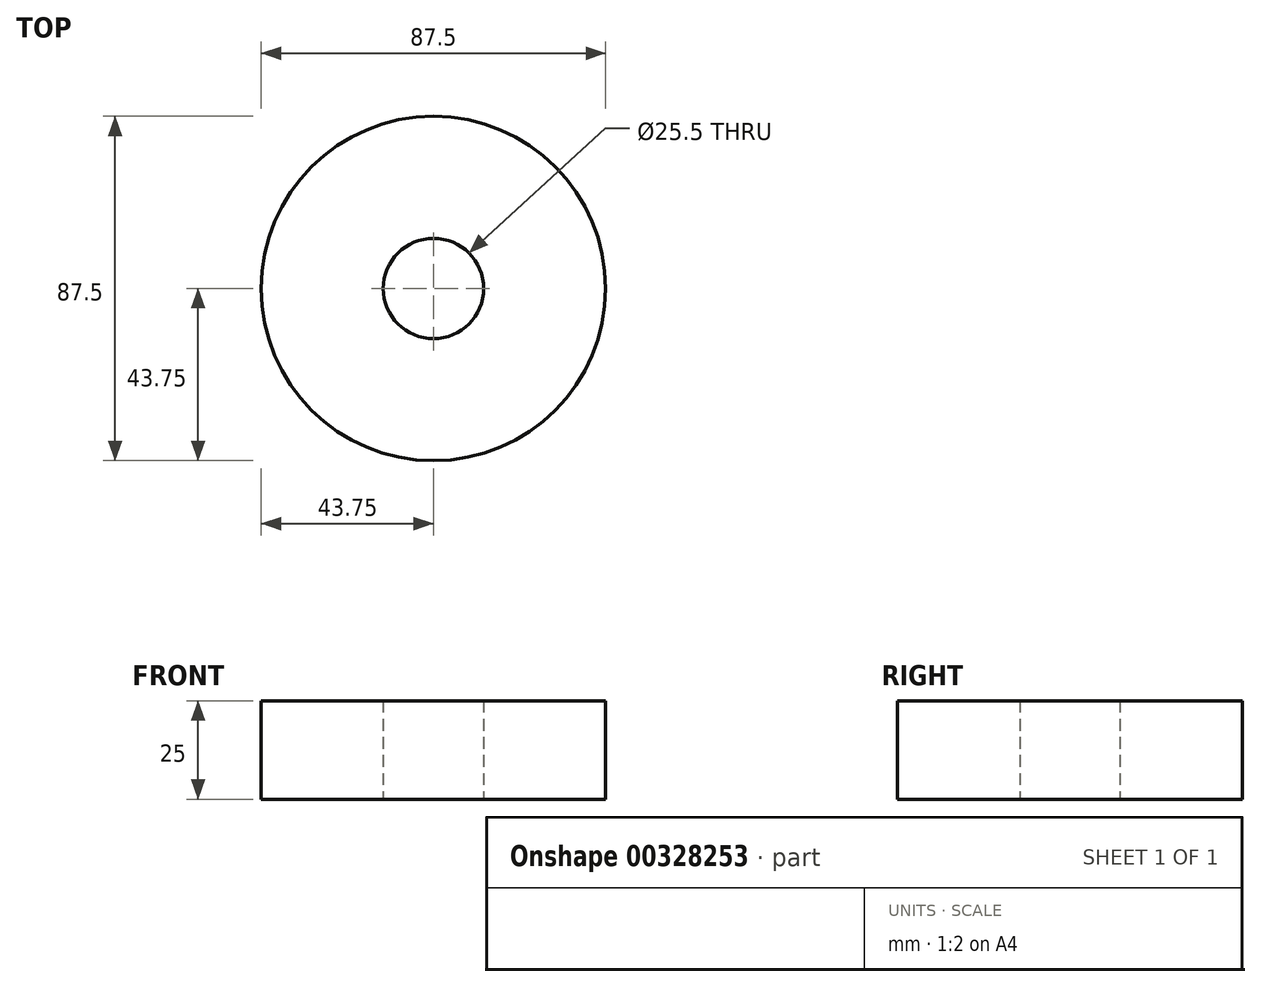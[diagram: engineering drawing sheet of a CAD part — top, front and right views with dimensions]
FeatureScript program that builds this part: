
annotation { "Feature Type Name" : "Feature", "Feature Type Description" : "" }
export const myFeature = defineFeature(function(context is Context, id is Id, definition is map)
    precondition{}
    {
        {
            var Q0;
            Q0=qCreatedBy(makeId("Top.planeOp"),FACE);
            var sketch = newSketch(context, id + "F0", { "sketchPlane" : qUnion([Q0])});
            skCircle(sketch, "E0", {"center": v(0, 0) * mm, "radius": 12.75 * mm});
            skCircle(sketch, "E1", {"center": v(0, 0) * mm, "radius": 43.75 * mm});
            skSolve(sketch);
        }
        {
            var Q0;
            Q0 = qSketchRegion(id + "F0", true);
            extrude(context, id + "F1", {"entities" : qUnion([Q0]), "depth" : 25 * mm});
        }
    });
